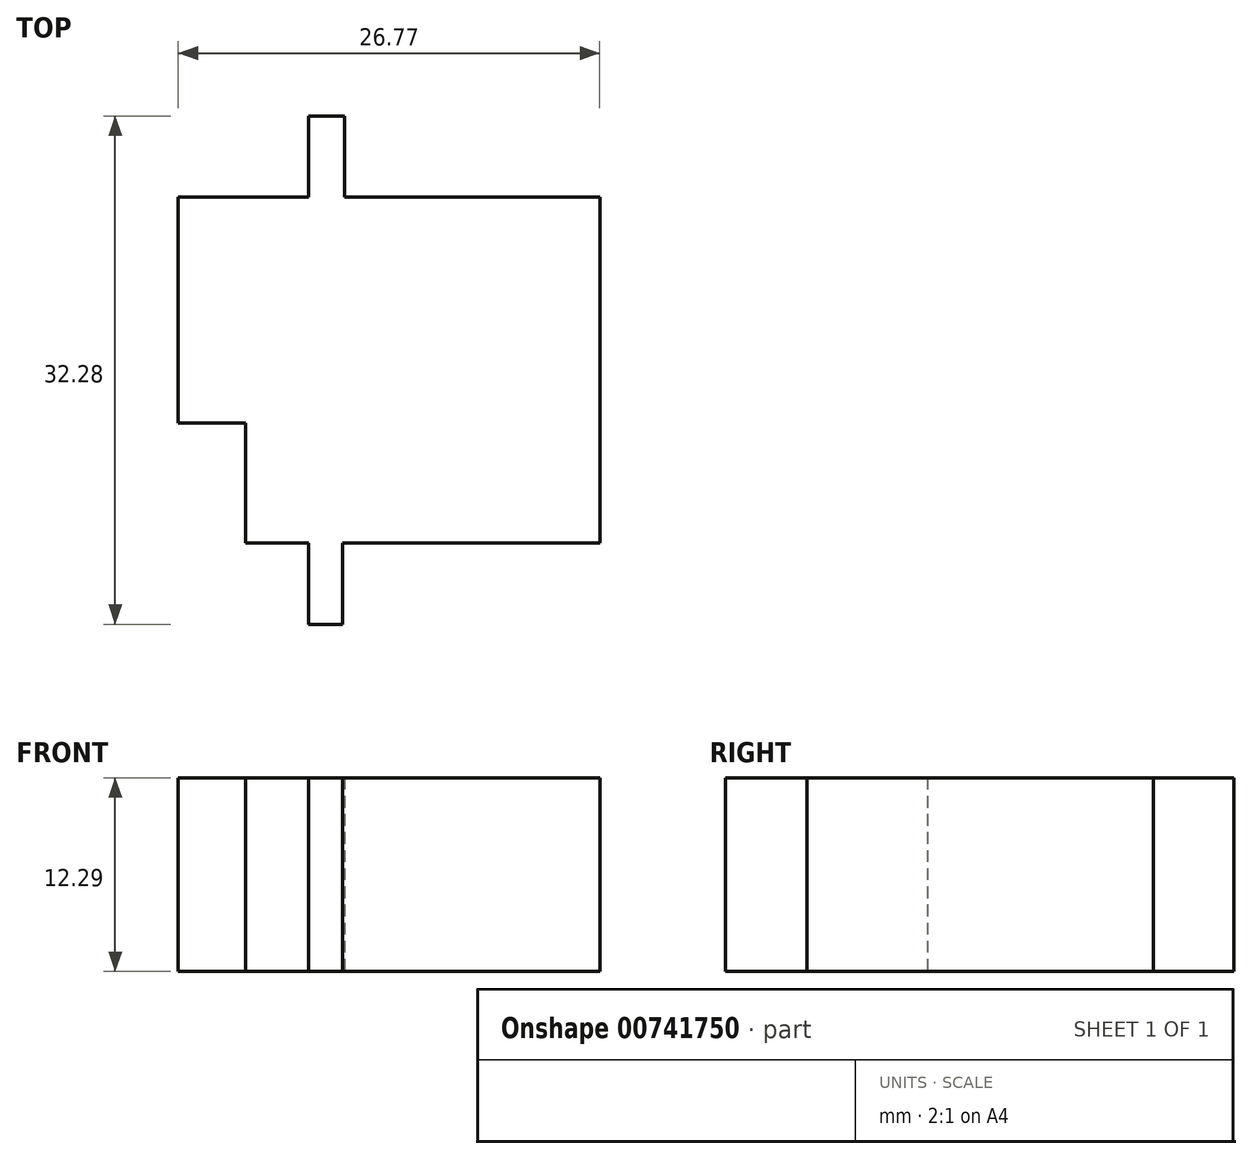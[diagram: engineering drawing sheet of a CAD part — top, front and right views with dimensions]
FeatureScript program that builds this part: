
annotation { "Feature Type Name" : "Feature", "Feature Type Description" : "" }
export const myFeature = defineFeature(function(context is Context, id is Id, definition is map)
    precondition{}
    {
        {
            var Q0;
            Q0=qCreatedBy(makeId("Top.planeOp"),FACE);
            var sketch = newSketch(context, id + "F0", { "sketchPlane" : qUnion([Q0])});
            skLineSegment(sketch, "E0.bottom", {"start": v(-18, 14.35) * mm, "end": v(4.5, 14.35) * mm});
            skLineSegment(sketch, "E0.top", {"start": v(-18, -7.65) * mm, "end": v(4.5, -7.65) * mm});
            skLineSegment(sketch, "E0.left", {"start": v(-18, 14.35) * mm, "end": v(-18, -7.65) * mm});
            skLineSegment(sketch, "E0.right", {"start": v(4.5, 14.35) * mm, "end": v(4.5, -7.65) * mm});
            skLineSegment(sketch, "E1.bottom", {"start": v(-18, 14.35) * mm, "end": v(-22.27, 14.35) * mm});
            skLineSegment(sketch, "E1.top", {"start": v(-18, 0) * mm, "end": v(-22.27, 0) * mm});
            skLineSegment(sketch, "E1.left", {"start": v(-18, 14.35) * mm, "end": v(-18, 0) * mm});
            skLineSegment(sketch, "E1.right", {"start": v(-22.27, 14.35) * mm, "end": v(-22.27, 0) * mm});
            skLineSegment(sketch, "E2.bottom", {"start": v(-13.99, 14.35) * mm, "end": v(-11.7, 14.35) * mm});
            skLineSegment(sketch, "E2.top", {"start": v(-13.99, 19.48) * mm, "end": v(-11.7, 19.48) * mm});
            skLineSegment(sketch, "E2.left", {"start": v(-11.7, 14.35) * mm, "end": v(-11.7, 19.48) * mm});
            skLineSegment(sketch, "E2.right", {"start": v(-13.99, 14.35) * mm, "end": v(-13.99, 19.48) * mm});
            skLineSegment(sketch, "E3.bottom", {"start": v(-13.99, -7.65) * mm, "end": v(-11.83, -7.65) * mm});
            skLineSegment(sketch, "E3.top", {"start": v(-13.99, -12.8) * mm, "end": v(-11.83, -12.8) * mm});
            skLineSegment(sketch, "E3.left", {"start": v(-13.99, -7.65) * mm, "end": v(-13.99, -12.8) * mm});
            skLineSegment(sketch, "E3.right", {"start": v(-11.83, -7.65) * mm, "end": v(-11.83, -12.8) * mm});
            skSolve(sketch);
        }
        {
            var Q0;
            {var subQ2=sQuery(id+"F0.wireOp",EDGE,"E0.right");Q0=makeQuery(id+"F0.imprint","IMPRINT",FACE,{"disambiguationData":[TD([[makeQuery(id+"F0.imprint","IMPRINT",EDGE,{"derivedFrom":subQ2}),-1.0]])]});}
            var Q1;
            {var subQ0=sQuery(id+"F0.wireOp",EDGE,"E1.bottom");Q1=makeQuery(id+"F0.imprint","IMPRINT",FACE,{"disambiguationData":[TD([[makeQuery(id+"F0.imprint","IMPRINT",EDGE,{"derivedFrom":subQ0}),1.0]])]});}
            var Q2;
            Q2=makeQuery(id+"F0.imprint","IMPRINT",FACE,{"disambiguationData":[TD([[makeQuery(id+"F0.imprint","IMPRINT",EDGE,{"derivedFrom":sQuery(id+"F0.wireOp",EDGE,"E2.top")}),-1.0]])]});
            var Q3;
            Q3=makeQuery(id+"F0.imprint","IMPRINT",FACE,{"disambiguationData":[TD([[makeQuery(id+"F0.imprint","IMPRINT",EDGE,{"derivedFrom":sQuery(id+"F0.wireOp",EDGE,"E3.top")}),1.0]])]});
            extrude(context, id + "F1", {"entities" : qUnion([Q0, Q1, Q2, Q3]), "depth" : 12.3 * mm, "offsetDistance" : 25.4 * mm});
        }
    });
